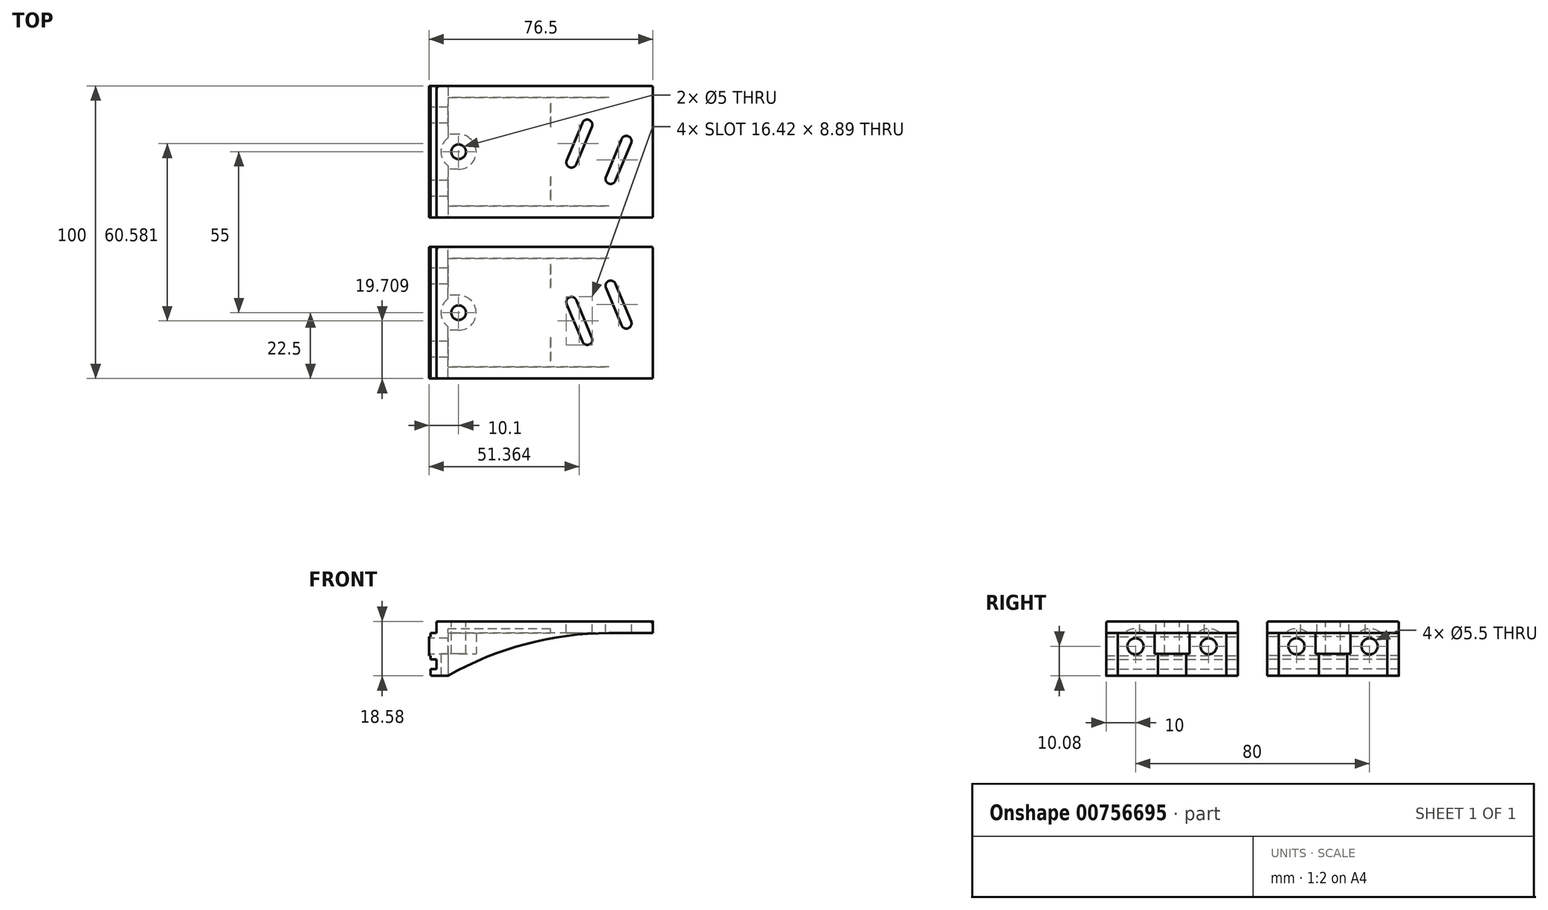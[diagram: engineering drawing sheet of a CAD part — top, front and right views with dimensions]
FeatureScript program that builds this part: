
annotation { "Feature Type Name" : "Feature", "Feature Type Description" : "" }
export const myFeature = defineFeature(function(context is Context, id is Id, definition is map)
    precondition{}
    {
        {
            var Q0;
            Q0=qCreatedBy(makeId("Front.planeOp"),FACE);
            var sketch = newSketch(context, id + "F0", { "sketchPlane" : qUnion([Q0])});
            skLineSegment(sketch, "E0", {"start": v(-0.5, 0) * mm, "end": v(-0.5, 3.25) * mm});
            skLineSegment(sketch, "E1", {"start": v(-0.5, 3.25) * mm, "end": v(0, 3.25) * mm});
            skLineSegment(sketch, "E2", {"start": v(0, 4.5) * mm, "end": v(2, 4.5) * mm});
            skLineSegment(sketch, "E3", {"start": v(2, 4.5) * mm, "end": v(2, 8.5) * mm});
            skLineSegment(sketch, "E4", {"start": v(2, 8.5) * mm, "end": v(6, 8.5) * mm});
            skLineSegment(sketch, "E5", {"start": v(6, 8.5) * mm, "end": v(6, 0) * mm});
            skLineSegment(sketch, "E6", {"start": v(-9.5, 0) * mm, "end": v(-9.5, 3.38) * mm, "construction": true});
            skLineSegment(sketch, "E7", {"start": v(-9.5, 3.38) * mm, "end": v(0, 3.38) * mm, "construction": true});
            skLineSegment(sketch, "E8", {"start": v(0, 3.38) * mm, "end": v(0, 4.87) * mm, "construction": true});
            skLineSegment(sketch, "E9", {"start": v(0, 4.87) * mm, "end": v(1.75, 4.87) * mm, "construction": true});
            skLineSegment(sketch, "E10", {"start": v(1.75, 4.87) * mm, "end": v(1.75, 8.47) * mm, "construction": true});
            skLineSegment(sketch, "E11", {"start": v(1.75, 8.47) * mm, "end": v(-22.36, 8.47) * mm, "construction": true});
            skLineSegment(sketch, "E12", {"start": v(0, 4.5) * mm, "end": v(0, 3.25) * mm});
            skLineSegment(sketch, "E13", {"start": v(-9.5, 0) * mm, "end": v(29.9, 0) * mm, "construction": true});
            skLineSegment(sketch, "E14.MirrorCS", {"start": v(-9.5, 0) * mm, "end": v(-9.5, -3.38) * mm, "construction": true});
            skLineSegment(sketch, "E15.MirrorCS", {"start": v(-9.5, -3.38) * mm, "end": v(0, -3.38) * mm, "construction": true});
            skLineSegment(sketch, "E16", {"start": v(0, -3.38) * mm, "end": v(0, -4.87) * mm, "construction": true});
            skLineSegment(sketch, "E17.MirrorCS", {"start": v(-0.5, 0) * mm, "end": v(-0.5, -3.25) * mm});
            skLineSegment(sketch, "E18.MirrorCS", {"start": v(-0.5, -3.25) * mm, "end": v(0, -3.25) * mm});
            skLineSegment(sketch, "E19", {"start": v(1.75, -4.87) * mm, "end": v(1.75, -7.47) * mm, "construction": true});
            skLineSegment(sketch, "E20", {"start": v(1.75, -7.47) * mm, "end": v(0, -7.47) * mm, "construction": true});
            skLineSegment(sketch, "E21", {"start": v(0, -7.47) * mm, "end": v(0, -10.07) * mm, "construction": true});
            skLineSegment(sketch, "E22", {"start": v(0, -10.07) * mm, "end": v(-21.5, -10.08) * mm, "construction": true});
            skLineSegment(sketch, "E23.MirrorCS", {"start": v(0, -4.5) * mm, "end": v(0, -3.25) * mm});
            skLineSegment(sketch, "E24.MirrorCS", {"start": v(0, -4.5) * mm, "end": v(2, -4.5) * mm});
            skLineSegment(sketch, "E25", {"start": v(2, -4.5) * mm, "end": v(2, -7.75) * mm});
            skLineSegment(sketch, "E26", {"start": v(2, -7.75) * mm, "end": v(0, -7.75) * mm});
            skLineSegment(sketch, "E27", {"start": v(0, -7.75) * mm, "end": v(0, -10.07) * mm});
            skLineSegment(sketch, "E28", {"start": v(0, -10.07) * mm, "end": v(6, -10.07) * mm});
            skLineSegment(sketch, "E29", {"start": v(6, -10.08) * mm, "end": v(6, 0) * mm});
            skLineSegment(sketch, "E30.MirrorCS", {"start": v(0, -4.87) * mm, "end": v(1.75, -4.87) * mm, "construction": true});
            skSolve(sketch);
        }
        {
            var Q0;
            Q0=qSketchRegion(id+"F0",true);
            extrude(context, id + "F1", {"entities" : qUnion([Q0]), "depth" : 22.5 * mm, "offsetDistance" : 25 * mm, "hasSecondDirection" : true, "secondDirectionOppositeDirection" : true, "secondDirectionDepth" : 22.5 * mm});
        }
        {
            var Q0;
            Q0=makeQuery(id+"F1.opExtrude","SWEPT_FACE",FACE,{"disambiguationData":[OSD([sQuery(id+"F0.wireOp",EDGE,"E5"),sQuery(id+"F0.wireOp",EDGE,"E29")])]});
            cPlane(context, id + "F2", {"entities" : qUnion([Q0]), "cplaneType" : CPlaneType.OFFSET, "offset" : 0 * mm, "width" : 150 * mm, "height" : 150 * mm});
        }
        {
            var Q0;
            Q0=qCreatedBy(makeId("Front.planeOp"),FACE);
            var sketch = newSketch(context, id + "F3", { "sketchPlane" : qUnion([Q0])});
            skLineSegment(sketch, "E31.0", {"start": v(6, 8.5) * mm, "end": v(6, -10.07) * mm});
            skLineSegment(sketch, "E32", {"start": v(6, 8.5) * mm, "end": v(76, 8.5) * mm});
            skLineSegment(sketch, "E33", {"start": v(76, 8.5) * mm, "end": v(76, 4.5) * mm});
            skLineSegment(sketch, "E34", {"start": v(76, 4.5) * mm, "end": v(6, 4.5) * mm, "construction": true});
            skArc(sketch, "E35", {"start": v(61, 4.5) * mm, "mid": v(32.55, 0.8) * mm, "end": v(6, -10.08) * mm});
            skLineSegment(sketch, "E36", {"start": v(61, 4.5) * mm, "end": v(76, 4.5) * mm});
            skSolve(sketch);
        }
        {
            var Q0;
            Q0=qSketchRegion(id+"F3",true);
            var Q1;
            Q1=makeQuery(id+"F1.opExtrude","CAP_FACE",FACE,{"disambiguationData":[OSD([sQuery(id+"F0.wireOp",EDGE,"E0"),sQuery(id+"F0.wireOp",EDGE,"E1"),sQuery(id+"F0.wireOp",EDGE,"E2"),sQuery(id+"F0.wireOp",EDGE,"E3"),sQuery(id+"F0.wireOp",EDGE,"E4"),sQuery(id+"F0.wireOp",EDGE,"E5"),sQuery(id+"F0.wireOp",EDGE,"E12"),sQuery(id+"F0.wireOp",EDGE,"E17.MirrorCS"),sQuery(id+"F0.wireOp",EDGE,"E18.MirrorCS"),sQuery(id+"F0.wireOp",EDGE,"E23.MirrorCS"),sQuery(id+"F0.wireOp",EDGE,"E24.MirrorCS"),sQuery(id+"F0.wireOp",EDGE,"E25"),sQuery(id+"F0.wireOp",EDGE,"E26"),sQuery(id+"F0.wireOp",EDGE,"E27"),sQuery(id+"F0.wireOp",EDGE,"E28"),sQuery(id+"F0.wireOp",EDGE,"E29")])],"isStart":false});
            var Q2;
            Q2=makeQuery(id+"F1.opExtrude","CAP_FACE",FACE,{"disambiguationData":[OSD([sQuery(id+"F0.wireOp",EDGE,"E0"),sQuery(id+"F0.wireOp",EDGE,"E1"),sQuery(id+"F0.wireOp",EDGE,"E2"),sQuery(id+"F0.wireOp",EDGE,"E3"),sQuery(id+"F0.wireOp",EDGE,"E4"),sQuery(id+"F0.wireOp",EDGE,"E5"),sQuery(id+"F0.wireOp",EDGE,"E12"),sQuery(id+"F0.wireOp",EDGE,"E17.MirrorCS"),sQuery(id+"F0.wireOp",EDGE,"E18.MirrorCS"),sQuery(id+"F0.wireOp",EDGE,"E23.MirrorCS"),sQuery(id+"F0.wireOp",EDGE,"E24.MirrorCS"),sQuery(id+"F0.wireOp",EDGE,"E25"),sQuery(id+"F0.wireOp",EDGE,"E26"),sQuery(id+"F0.wireOp",EDGE,"E27"),sQuery(id+"F0.wireOp",EDGE,"E28"),sQuery(id+"F0.wireOp",EDGE,"E29")])],"isStart":true});
            extrude(context, id + "F4", {"entities" : qUnion([Q0]), "operationType" : NewBodyOperationType.ADD, "endBound" : BoundingType.UP_TO_SURFACE, "depth" : 25 * mm, "endBoundEntityFace" : qUnion([Q1]), "offsetDistance" : 25 * mm, "hasSecondDirection" : true, "secondDirectionBound" : SecondDirectionBoundingType.UP_TO_SURFACE, "secondDirectionOppositeDirection" : true, "secondDirectionDepth" : 25 * mm, "secondDirectionBoundEntityFace" : qUnion([Q2])});
        }
        {
            var Q0;
            Q0=qCreatedBy(id+"F2.planeOp",FACE);
            var sketch = newSketch(context, id + "F5", { "sketchPlane" : qUnion([Q0])});
            skLineSegment(sketch, "E37.0", {"start": v(-22.5, -10.07) * mm, "end": v(22.5, -10.07) * mm, "construction": true});
            skLineSegment(sketch, "E38.0", {"start": v(-22.5, 4.5) * mm, "end": v(22.5, 4.5) * mm, "construction": true});
            skLineSegment(sketch, "E39.bottom", {"start": v(-18.5, 4.5) * mm, "end": v(18.5, 4.5) * mm});
            skLineSegment(sketch, "E39.top", {"start": v(-18.5, -10.07) * mm, "end": v(18.5, -10.07) * mm});
            skLineSegment(sketch, "E39.left", {"start": v(-18.5, 4.5) * mm, "end": v(-18.5, -10.07) * mm});
            skLineSegment(sketch, "E39.right", {"start": v(18.5, 4.5) * mm, "end": v(18.5, -10.07) * mm});
            skLineSegment(sketch, "E40", {"start": v(0, 4.5) * mm, "end": v(0, -10.07) * mm, "construction": true});
            skSolve(sketch);
        }
        {
            var Q0;
            Q0 = qSketchRegion(id + "F5", true);
            extrude(context, id + "F6", {"entities" : qUnion([Q0]), "operationType" : NewBodyOperationType.REMOVE, "endBound" : BoundingType.THROUGH_ALL, "depth" : 25 * mm, "offsetDistance" : 25 * mm});
        }
        {
            var Q0;
            Q0=makeQuery(id+"F4.boolean.opBoolean","MERGE",FACE,{"derivedFrom":[makeQuery(id+"F1.opExtrude","SWEPT_FACE",FACE,{"disambiguationData":[OSD([sQuery(id+"F0.wireOp",EDGE,"E4")])]}),makeQuery(id+"F4.opExtrude","SWEPT_FACE",FACE,{"disambiguationData":[OSD([sQuery(id+"F3.wireOp",EDGE,"E32")])]})]});
            var sketch = newSketch(context, id + "F7", { "sketchPlane" : qUnion([Q0])});
            skCircle(sketch, "E41", {"center": v(9.6, 0) * mm, "radius": 2.5 * mm});
            skLineSegment(sketch, "E42", {"start": v(61.55, 9.25) * mm, "end": v(66.94, -3.67) * mm});
            skLineSegment(sketch, "E43", {"start": v(9.6, -20) * mm, "end": v(57.56, 0) * mm, "construction": true});
            skLineSegment(sketch, "E44", {"start": v(48.17, 3.67) * mm, "end": v(61.55, 9.25) * mm, "construction": true});
            skLineSegment(sketch, "E45.MirrorCS", {"start": v(53.56, -9.25) * mm, "end": v(66.94, -3.67) * mm, "construction": true});
            skArc(sketch, "E46.0.startCap", {"start": v(59.94, 8.58) * mm, "mid": v(60.88, 10.87) * mm, "end": v(63.17, 9.92) * mm});
            skArc(sketch, "E46.0.endCap", {"start": v(68.56, -3) * mm, "mid": v(67.61, -5.29) * mm, "end": v(65.33, -4.34) * mm});
            skLineSegment(sketch, "E46.0.left", {"start": v(63.17, 9.92) * mm, "end": v(68.56, -3) * mm});
            skLineSegment(sketch, "E46.0.right", {"start": v(59.94, 8.58) * mm, "end": v(65.33, -4.34) * mm});
            skLineSegment(sketch, "E47", {"start": v(9.6, 0) * mm, "end": v(9.6, -20) * mm, "construction": true});
            skPoint(sketch, "E48", {"position": v(30.56, -11.26) * mm});
            skPoint(sketch, "E49", {"position": v(12.1, -18.96) * mm});
            skCircle(sketch, "E50", {"center": v(9.6, 0) * mm, "radius": 7.5 * mm, "construction": true});
            skLineSegment(sketch, "E51", {"start": v(9.6, 0) * mm, "end": v(57.56, 0) * mm, "construction": true});
            skLineSegment(sketch, "E52", {"start": v(61.55, 9.25) * mm, "end": v(53.56, -9.25) * mm, "construction": true});
            skLineSegment(sketch, "E53", {"start": v(48.17, 3.67) * mm, "end": v(53.56, -9.25) * mm});
            skArc(sketch, "E54.0.startCap", {"start": v(46.55, 3) * mm, "mid": v(47.5, 5.29) * mm, "end": v(49.78, 4.34) * mm});
            skArc(sketch, "E54.0.endCap", {"start": v(55.17, -8.58) * mm, "mid": v(54.23, -10.87) * mm, "end": v(51.94, -9.92) * mm});
            skLineSegment(sketch, "E54.0.left", {"start": v(49.78, 4.34) * mm, "end": v(55.17, -8.58) * mm});
            skLineSegment(sketch, "E54.0.right", {"start": v(46.55, 3) * mm, "end": v(51.94, -9.92) * mm});
            skSolve(sketch);
        }
        {
            var Q0;
            Q0 = qSketchRegion(id + "F7", true);
            extrude(context, id + "F8", {"entities" : qUnion([Q0]), "operationType" : NewBodyOperationType.REMOVE, "endBound" : BoundingType.THROUGH_ALL, "oppositeDirection" : true, "depth" : 25 * mm, "offsetDistance" : 25 * mm});
        }
        {
            var Q0;
            Q0=makeQuery(id+"F1.opExtrude","SWEPT_FACE",FACE,{"disambiguationData":[OSD([sQuery(id+"F0.wireOp",EDGE,"E28")])]});
            var sketch = newSketch(context, id + "F9", { "sketchPlane" : qUnion([Q0])});
            skCircle(sketch, "E55.0", {"center": v(9.6, 0) * mm, "radius": 2.5 * mm, "construction": true});
            skCircle(sketch, "E56", {"center": v(9.6, 0) * mm, "radius": 6 * mm});
            skSolve(sketch);
        }
        {
            var Q0;
            Q0 = qSketchRegion(id + "F9", true);
            extrude(context, id + "F10", {"entities" : qUnion([Q0]), "operationType" : NewBodyOperationType.REMOVE, "oppositeDirection" : true, "depth" : 7.5 * mm, "offsetDistance" : 25 * mm});
        }
        {
            var Q0;
            Q0=makeQuery(id+"F1.opExtrude","SWEPT_FACE",FACE,{"disambiguationData":[OSD([sQuery(id+"F0.wireOp",EDGE,"E0"),sQuery(id+"F0.wireOp",EDGE,"E17.MirrorCS")])]});
            var sketch = newSketch(context, id + "F11", { "sketchPlane" : qUnion([Q0])});
            skCircle(sketch, "E57", {"center": v(-12.5, 0) * mm, "radius": 2.75 * mm});
            skCircle(sketch, "E58.MirrorC", {"center": v(12.5, 0) * mm, "radius": 2.75 * mm});
            skSolve(sketch);
        }
        {
            var Q0;
            Q0 = qSketchRegion(id + "F11", true);
            extrude(context, id + "F12", {"entities" : qUnion([Q0]), "operationType" : NewBodyOperationType.REMOVE, "endBound" : BoundingType.THROUGH_ALL, "oppositeDirection" : true, "depth" : 25 * mm, "offsetDistance" : 25 * mm});
        }
        {
            var Q0;
            Q0=makeQuery(id+"F10.boolean.opBoolean","COPY",FACE,{"derivedFrom":makeQuery(id+"F10.opExtrude","CAP_FACE",FACE,{"disambiguationData":[OSD([sQuery(id+"F9.wireOp",EDGE,"E56")])],"isStart":false})});
            var sketch = newSketch(context, id + "F13", { "sketchPlane" : qUnion([Q0])});
            skCircle(sketch, "E59.0", {"center": v(9.6, 0) * mm, "radius": 2.5 * mm});
            skCircle(sketch, "E60", {"center": v(9.6, 0) * mm, "radius": 6 * mm, "construction": true});
            skLineSegment(sketch, "E61", {"start": v(9.6, 6) * mm, "end": v(0, 6) * mm});
            skLineSegment(sketch, "E62", {"start": v(9.6, 6) * mm, "end": v(9.6, 0) * mm, "construction": true});
            skArc(sketch, "E63", {"start": v(15.6, 0) * mm, "mid": v(13.84, 4.24) * mm, "end": v(9.6, 6) * mm});
            skLineSegment(sketch, "E64", {"start": v(0, 6) * mm, "end": v(0, 0) * mm});
            skLineSegment(sketch, "E65.MirrorCS", {"start": v(0, -6) * mm, "end": v(0, 0) * mm});
            skLineSegment(sketch, "E66.MirrorCS", {"start": v(9.6, -6) * mm, "end": v(0, -6) * mm});
            skArc(sketch, "E67.MirrorCS", {"start": v(15.6, 0) * mm, "mid": v(13.84, -4.24) * mm, "end": v(9.6, -6) * mm});
            skSolve(sketch);
        }
        {
            var Q0;
            Q0 = qSketchRegion(id + "F13", true);
            var Q1;
            Q1=makeQuery(id+"F6.boolean.opBoolean","MERGE",FACE,{"derivedFrom":[makeQuery(id+"F4.opExtrude","SWEPT_FACE",FACE,{"disambiguationData":[OSD([sQuery(id+"F3.wireOp",EDGE,"E36")])]})],"fromTools":[makeQuery(id+"F6.opExtrude","SWEPT_FACE",FACE,{"disambiguationData":[OSD([sQuery(id+"F5.wireOp",EDGE,"E39.bottom")])]})]});
            extrude(context, id + "F14", {"entities" : qUnion([Q0]), "operationType" : NewBodyOperationType.ADD, "endBound" : BoundingType.UP_TO_SURFACE, "oppositeDirection" : true, "depth" : 25 * mm, "endBoundEntityFace" : qUnion([Q1]), "offsetDistance" : 25 * mm});
        }
        {
            var Q0;
            {var subQ0=sQuery(id+"F5.wireOp",EDGE,"E39.left");Q0=makeQuery(id+"F14.boolean.opBoolean","SPLIT",FACE,{"disambiguationData":[TD([makeQuery(id+"F6.boolean.opBoolean","COPY",FACE,{"derivedFrom":makeQuery(id+"F6.opExtrude","SWEPT_FACE",FACE,{"disambiguationData":[OSD([subQ0])]})})])],"derivedFrom":makeQuery(id+"F6.boolean.opBoolean","COPY",FACE,{"derivedFrom":makeQuery(id+"F6.opExtrude","CAP_FACE",FACE,{"disambiguationData":[OSD([sQuery(id+"F5.wireOp",EDGE,"E39.bottom"),sQuery(id+"F5.wireOp",EDGE,"E39.top"),subQ0,sQuery(id+"F5.wireOp",EDGE,"E39.right")])],"isStart":true})})});}
            var sketch = newSketch(context, id + "F15", { "sketchPlane" : qUnion([Q0])});
            skCircle(sketch, "E68", {"center": v(-12.5, 0) * mm, "radius": 6 * mm});
            skCircle(sketch, "E69.MirrorC", {"center": v(12.5, 0) * mm, "radius": 6 * mm});
            skSolve(sketch);
        }
        {
            var Q0;
            Q0 = qSketchRegion(id + "F15", true);
            extrude(context, id + "F16", {"entities" : qUnion([Q0]), "operationType" : NewBodyOperationType.REMOVE, "depth" : 35 * mm, "offsetDistance" : 25 * mm});
        }
        {
            var Q0;
            Q0=makeQuery(id+"F1.opExtrude","SWEPT_EDGE",EDGE,{"disambiguationData":[OSD([sQuery(id+"F0.wireOp",EDGE,"E3"),sQuery(id+"F0.wireOp",EDGE,"E4")])]});
            var Q1;
            Q1=makeQuery(id+"F4.boolean.opBoolean","MERGE",EDGE,{"derivedFrom":[makeQuery(id+"F1.opExtrude","CAP_EDGE",EDGE,{"disambiguationData":[OSD([sQuery(id+"F0.wireOp",EDGE,"E4")])],"isStart":false}),makeQuery(id+"F4.opExtrude","CAP_EDGE",EDGE,{"disambiguationData":[OSD([sQuery(id+"F3.wireOp",EDGE,"E32")])],"isStart":false})]});
            var Q2;
            Q2=makeQuery(id+"F4.boolean.opBoolean","MERGE",EDGE,{"derivedFrom":[makeQuery(id+"F1.opExtrude","CAP_EDGE",EDGE,{"disambiguationData":[OSD([sQuery(id+"F0.wireOp",EDGE,"E4")])],"isStart":true}),makeQuery(id+"F4.opExtrude","CAP_EDGE",EDGE,{"disambiguationData":[OSD([sQuery(id+"F3.wireOp",EDGE,"E32")])],"isStart":true})]});
            var Q3;
            Q3=makeQuery(id+"F4.opExtrude","TWEAK_EDGE",EDGE,{"derivedFrom":[makeQuery(id+"F3.imprint","IMPRINT",EDGE,{"derivedFrom":sQuery(id+"F3.wireOp",EDGE,"E32")}),makeQuery(id+"F3.imprint","IMPRINT",EDGE,{"derivedFrom":sQuery(id+"F3.wireOp",EDGE,"E33")})]});
            var Q4;
            Q4=makeQuery(id+"F4.opExtrude","CAP_EDGE",EDGE,{"disambiguationData":[OSD([sQuery(id+"F3.wireOp",EDGE,"E35")])],"isStart":false});
            var Q5;
            Q5=makeQuery(id+"F4.opExtrude","CAP_EDGE",EDGE,{"disambiguationData":[OSD([sQuery(id+"F3.wireOp",EDGE,"E35")])],"isStart":true});
            var Q6;
            Q6=makeQuery(id+"F1.opExtrude","SWEPT_EDGE",EDGE,{"disambiguationData":[OSD([sQuery(id+"F0.wireOp",EDGE,"E27"),sQuery(id+"F0.wireOp",EDGE,"E28")])]});
            var Q7;
            Q7=makeQuery(id+"F4.opExtrude","CAP_EDGE",EDGE,{"disambiguationData":[OSD([sQuery(id+"F3.wireOp",EDGE,"E33")])],"isStart":true});
            var Q8;
            Q8=makeQuery(id+"F4.opExtrude","CAP_EDGE",EDGE,{"disambiguationData":[OSD([sQuery(id+"F3.wireOp",EDGE,"E33")])],"isStart":false});
            var Q9;
            Q9=makeQuery(id+"F4.opExtrude","TWEAK_EDGE",EDGE,{"derivedFrom":[makeQuery(id+"F3.imprint","IMPRINT",EDGE,{"derivedFrom":sQuery(id+"F3.wireOp",EDGE,"E33")}),makeQuery(id+"F3.imprint","IMPRINT",EDGE,{"derivedFrom":sQuery(id+"F3.wireOp",EDGE,"E36")})]});
            var Q10;
            {var subQ0=makeQuery(id+"F16.opExtrude","SWEPT_FACE",FACE,{"disambiguationData":[OSD([sQuery(id+"F15.wireOp",EDGE,"E68")])]});var subQ1=makeQuery(id+"F6.boolean.opBoolean","MERGE",FACE,{"derivedFrom":[makeQuery(id+"F4.opExtrude","SWEPT_FACE",FACE,{"disambiguationData":[OSD([sQuery(id+"F3.wireOp",EDGE,"E36")])]})],"fromTools":[makeQuery(id+"F6.opExtrude","SWEPT_FACE",FACE,{"disambiguationData":[OSD([sQuery(id+"F5.wireOp",EDGE,"E39.bottom")])]})]});Q10=qUnion([makeQuery(id+"F16.boolean.opBoolean","INTERSECT",EDGE,{"disambiguationData":[OD(0.0)],"derivedFrom":[subQ1,subQ0]}),makeQuery(id+"F16.boolean.opBoolean","INTERSECT",EDGE,{"disambiguationData":[OD(1.0)],"derivedFrom":[subQ1,subQ0]})]);}
            var Q11;
            Q11=makeQuery(id+"F4.opExtrude","TWEAK_EDGE",EDGE,{"derivedFrom":[makeQuery(id+"F3.imprint","IMPRINT",EDGE,{"derivedFrom":sQuery(id+"F3.wireOp",EDGE,"E33")}),makeQuery(id+"F3.imprint","IMPRINT",EDGE,{"derivedFrom":sQuery(id+"F3.wireOp",EDGE,"E36")})]});
            var Q12;
            Q12=makeQuery(id+"F4.opExtrude","TWEAK_EDGE",EDGE,{"derivedFrom":[makeQuery(id+"F3.imprint","IMPRINT",EDGE,{"derivedFrom":sQuery(id+"F3.wireOp",EDGE,"E33")}),makeQuery(id+"F3.imprint","IMPRINT",EDGE,{"derivedFrom":sQuery(id+"F3.wireOp",EDGE,"E36")})]});
            var Q13;
            {var subQ0=makeQuery(id+"F16.opExtrude","SWEPT_FACE",FACE,{"disambiguationData":[OSD([sQuery(id+"F15.wireOp",EDGE,"E69.MirrorC")])]});var subQ1=makeQuery(id+"F6.boolean.opBoolean","MERGE",FACE,{"derivedFrom":[makeQuery(id+"F4.opExtrude","SWEPT_FACE",FACE,{"disambiguationData":[OSD([sQuery(id+"F3.wireOp",EDGE,"E36")])]})],"fromTools":[makeQuery(id+"F6.opExtrude","SWEPT_FACE",FACE,{"disambiguationData":[OSD([sQuery(id+"F5.wireOp",EDGE,"E39.bottom")])]})]});Q13=qUnion([makeQuery(id+"F16.boolean.opBoolean","INTERSECT",EDGE,{"disambiguationData":[OD(0.0)],"derivedFrom":[subQ1,subQ0]}),makeQuery(id+"F16.boolean.opBoolean","INTERSECT",EDGE,{"disambiguationData":[OD(1.0)],"derivedFrom":[subQ1,subQ0]})]);}
            fillet(context, id + "F17", {"entities" : qUnion([Q0, Q1, Q2, Q3, Q4, Q5, Q6, Q7, Q8, Q9, Q10, Q11, Q12, Q13]), "radius" : 0.5 * mm, "tangentPropagation" : true, "allowEdgeOverflow" : false});
        }
        {
            var Q0;
            Q0=makeQuery(id+"F4.boolean.opBoolean","MERGE",FACE,{"derivedFrom":[makeQuery(id+"F1.opExtrude","CAP_FACE",FACE,{"disambiguationData":[OSD([sQuery(id+"F0.wireOp",EDGE,"E0"),sQuery(id+"F0.wireOp",EDGE,"E1"),sQuery(id+"F0.wireOp",EDGE,"E2"),sQuery(id+"F0.wireOp",EDGE,"E3"),sQuery(id+"F0.wireOp",EDGE,"E4"),sQuery(id+"F0.wireOp",EDGE,"E5"),sQuery(id+"F0.wireOp",EDGE,"E12"),sQuery(id+"F0.wireOp",EDGE,"E17.MirrorCS"),sQuery(id+"F0.wireOp",EDGE,"E18.MirrorCS"),sQuery(id+"F0.wireOp",EDGE,"E23.MirrorCS"),sQuery(id+"F0.wireOp",EDGE,"E24.MirrorCS"),sQuery(id+"F0.wireOp",EDGE,"E25"),sQuery(id+"F0.wireOp",EDGE,"E26"),sQuery(id+"F0.wireOp",EDGE,"E27"),sQuery(id+"F0.wireOp",EDGE,"E28"),sQuery(id+"F0.wireOp",EDGE,"E29")])],"isStart":true}),makeQuery(id+"F4.opExtrude","CAP_FACE",FACE,{"disambiguationData":[OSD([sQuery(id+"F3.wireOp",EDGE,"E31.0"),sQuery(id+"F3.wireOp",EDGE,"E32"),sQuery(id+"F3.wireOp",EDGE,"E33"),sQuery(id+"F3.wireOp",EDGE,"E35"),sQuery(id+"F3.wireOp",EDGE,"E36")])],"isStart":true})]});
            cPlane(context, id + "F18", {"entities" : qUnion([Q0]), "cplaneType" : CPlaneType.OFFSET, "offset" : 5 * mm, "width" : 150 * mm, "height" : 150 * mm});
        }
        {
            var Q0;
            Q0=makeQuery(id+"F1.opExtrude","SWEPT_BODY",BODY,{"disambiguationData":[OSD([sQuery(id+"F0.wireOp",EDGE,"E0"),sQuery(id+"F0.wireOp",EDGE,"E1"),sQuery(id+"F0.wireOp",EDGE,"E2"),sQuery(id+"F0.wireOp",EDGE,"E3"),sQuery(id+"F0.wireOp",EDGE,"E4"),sQuery(id+"F0.wireOp",EDGE,"E5"),sQuery(id+"F0.wireOp",EDGE,"E12"),sQuery(id+"F0.wireOp",EDGE,"E17.MirrorCS"),sQuery(id+"F0.wireOp",EDGE,"E18.MirrorCS"),sQuery(id+"F0.wireOp",EDGE,"E23.MirrorCS"),sQuery(id+"F0.wireOp",EDGE,"E24.MirrorCS"),sQuery(id+"F0.wireOp",EDGE,"E25"),sQuery(id+"F0.wireOp",EDGE,"E26"),sQuery(id+"F0.wireOp",EDGE,"E27"),sQuery(id+"F0.wireOp",EDGE,"E28"),sQuery(id+"F0.wireOp",EDGE,"E29")])]});
            var Q1;
            Q1=qCreatedBy(id+"F18.planeOp",FACE);
            mirror(context, id + "F19", {"entities" : qUnion([Q0]), "mirrorPlane" : qUnion([Q1])});
        }
    });
